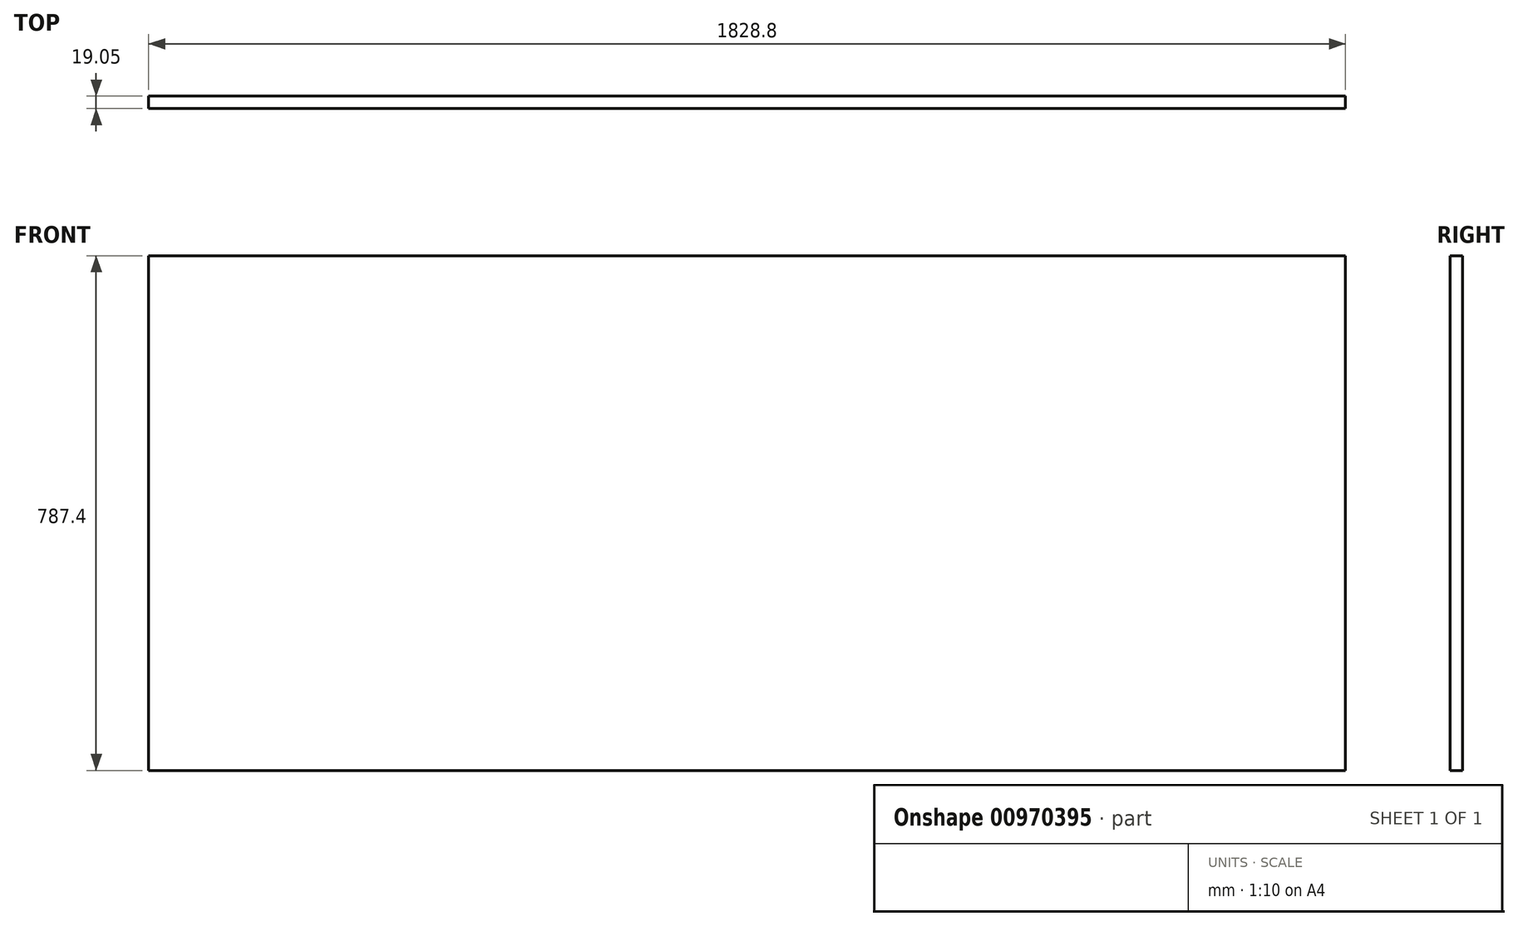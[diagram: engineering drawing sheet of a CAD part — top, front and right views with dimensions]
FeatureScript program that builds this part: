
annotation { "Feature Type Name" : "Feature", "Feature Type Description" : "" }
export const myFeature = defineFeature(function(context is Context, id is Id, definition is map)
    precondition{}
    {
        {
            var Q0;
            Q0=qCreatedBy(makeId("Front.planeOp"),FACE);
            var sketch = newSketch(context, id + "F0", { "sketchPlane" : qUnion([Q0])});
            skLineSegment(sketch, "E0.bottom", {"start": v(0, 0) * mm, "end": v(1828.8, 0) * mm});
            skLineSegment(sketch, "E0.top", {"start": v(0, -787.4) * mm, "end": v(1828.8, -787.4) * mm});
            skLineSegment(sketch, "E0.left", {"start": v(0, 0) * mm, "end": v(0, -787.4) * mm});
            skLineSegment(sketch, "E0.right", {"start": v(1828.8, 0) * mm, "end": v(1828.8, -787.4) * mm});
            skSolve(sketch);
        }
        {
            var Q0;
            Q0 = qSketchRegion(id + "F0", true);
            extrude(context, id + "F1", {"entities" : qUnion([Q0]), "depth" : 19.05 * mm, "offsetDistance" : 25.4 * mm});
        }
    });
